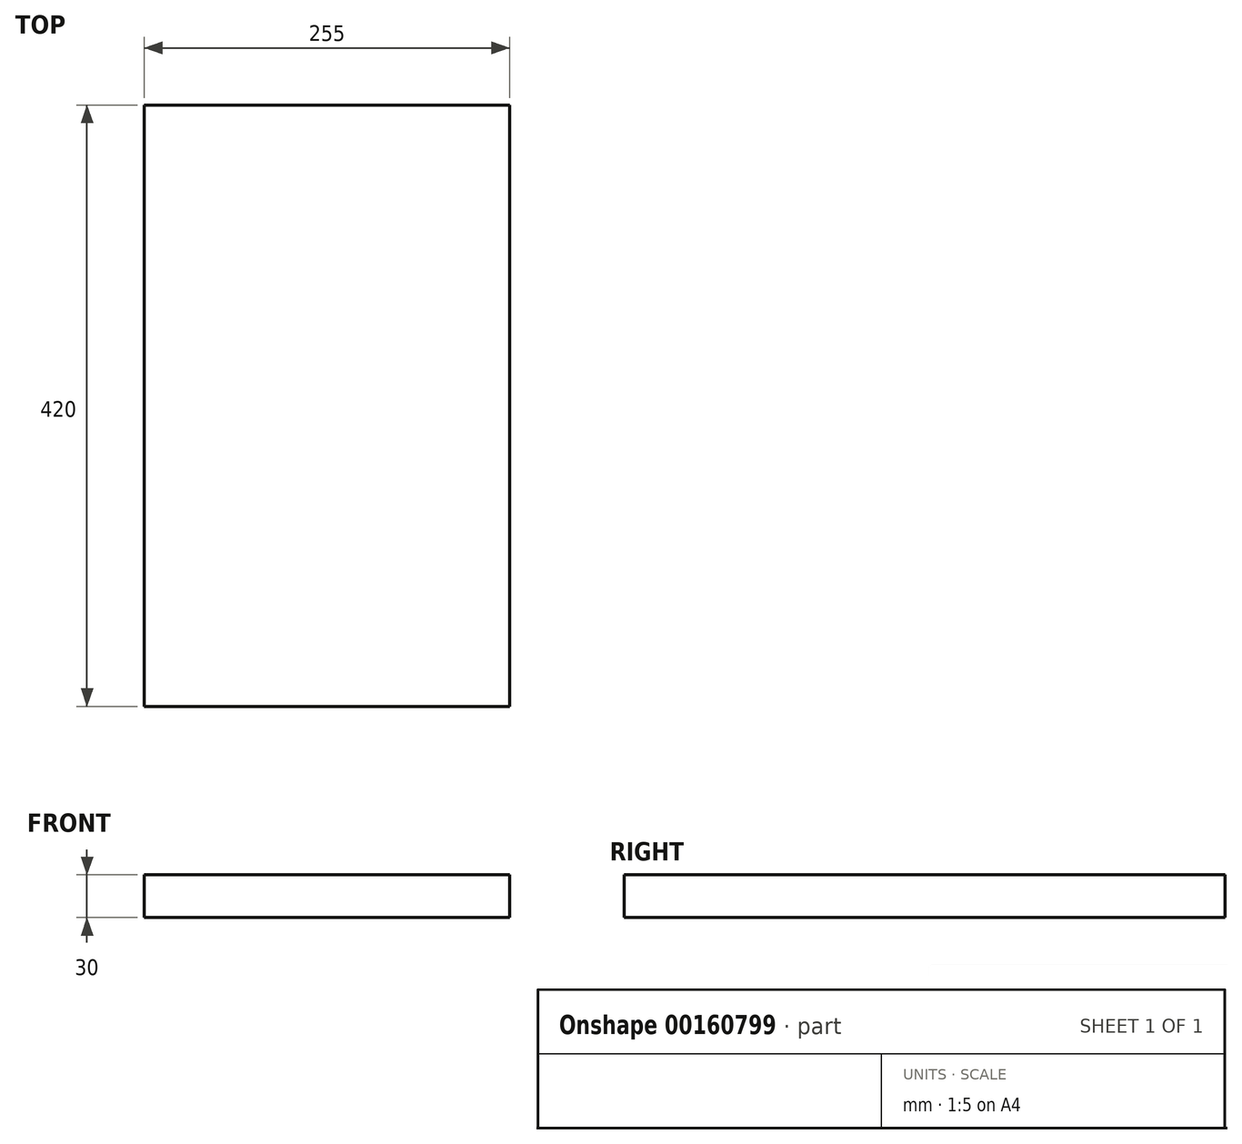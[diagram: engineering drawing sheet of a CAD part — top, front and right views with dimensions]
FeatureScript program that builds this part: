
annotation { "Feature Type Name" : "Feature", "Feature Type Description" : "" }
export const myFeature = defineFeature(function(context is Context, id is Id, definition is map)
    precondition{}
    {
        {
            var Q0;
            Q0=qCreatedBy(makeId("Front.planeOp"),FACE);
            var sketch = newSketch(context, id + "F0", { "sketchPlane" : qUnion([Q0])});
            skLineSegment(sketch, "E0.bottom", {"start": v(-239.08, 19.85) * mm, "end": v(15.92, 19.85) * mm});
            skLineSegment(sketch, "E0.top", {"start": v(-239.08, -10.15) * mm, "end": v(15.92, -10.15) * mm});
            skLineSegment(sketch, "E0.left", {"start": v(-239.08, 19.85) * mm, "end": v(-239.08, -10.15) * mm});
            skLineSegment(sketch, "E0.right", {"start": v(15.92, 19.85) * mm, "end": v(15.92, -10.15) * mm});
            skSolve(sketch);
        }
        {
            var Q0;
            Q0=makeQuery(id+"F0.imprint","IMPRINT",FACE,{"disambiguationData":[TD([[makeQuery(id+"F0.imprint","IMPRINT",EDGE,{"derivedFrom":sQuery(id+"F0.wireOp",EDGE,"E0.bottom")}),-1.0]])]});
            extrude(context, id + "F1", {"entities" : qUnion([Q0]), "depth" : 420 * mm});
        }
    });
